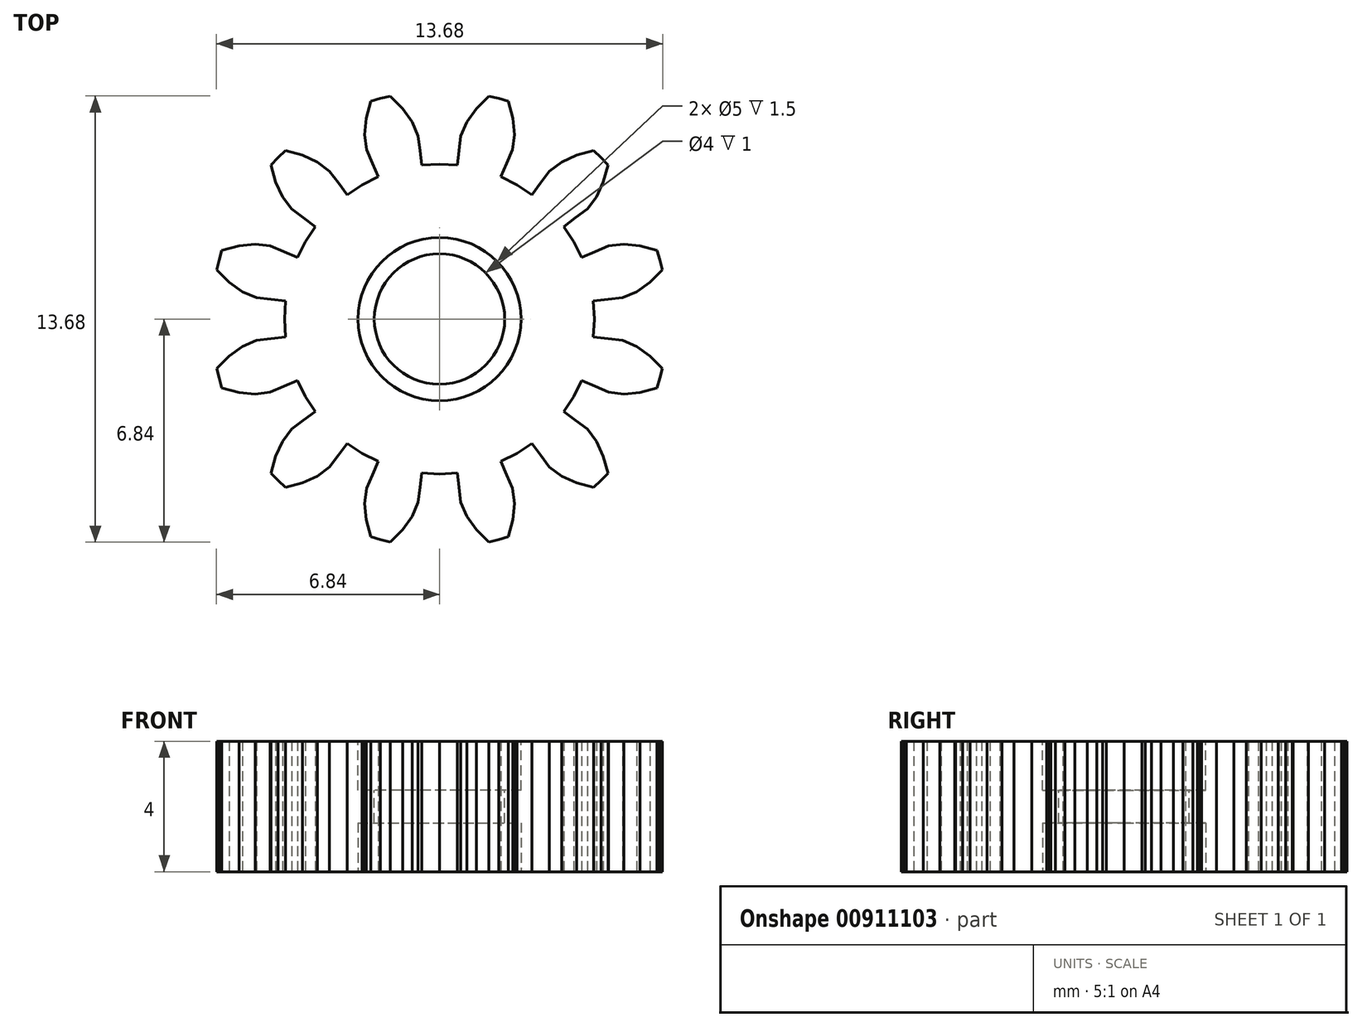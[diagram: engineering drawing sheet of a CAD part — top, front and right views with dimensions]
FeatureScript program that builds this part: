
annotation { "Feature Type Name" : "Feature", "Feature Type Description" : "" }
export const myFeature = defineFeature(function(context is Context, id is Id, definition is map)
    precondition{}
    {
        {
            var Q0;
            Q0=qCreatedBy(makeId("Top.planeOp"),FACE);
            var sketch = newSketch(context, id + "F0", { "sketchPlane" : qUnion([Q0])});
            skLineSegment(sketch, "E0", {"start": v(4.75, 0) * mm, "end": v(4.72, 0.55) * mm});
            skLineSegment(sketch, "E1", {"start": v(4.72, 0.55) * mm, "end": v(5.17, 0.6) * mm});
            skLineSegment(sketch, "E2", {"start": v(5.17, 0.6) * mm, "end": v(5.61, 0.65) * mm});
            skLineSegment(sketch, "E3", {"start": v(5.61, 0.65) * mm, "end": v(6.04, 0.84) * mm});
            skLineSegment(sketch, "E4", {"start": v(6.04, 0.84) * mm, "end": v(6.45, 1.13) * mm});
            skLineSegment(sketch, "E5", {"start": v(6.45, 1.13) * mm, "end": v(6.84, 1.51) * mm});
            skLineSegment(sketch, "E6", {"start": v(6.84, 1.51) * mm, "end": v(6.76, 1.81) * mm});
            skLineSegment(sketch, "E7", {"start": v(6.76, 1.81) * mm, "end": v(6.67, 2.1) * mm});
            skLineSegment(sketch, "E8", {"start": v(6.67, 2.1) * mm, "end": v(6.15, 2.25) * mm});
            skLineSegment(sketch, "E9", {"start": v(6.15, 2.25) * mm, "end": v(5.65, 2.3) * mm});
            skLineSegment(sketch, "E10", {"start": v(5.65, 2.3) * mm, "end": v(5.19, 2.24) * mm});
            skLineSegment(sketch, "E11", {"start": v(5.19, 2.24) * mm, "end": v(4.77, 2.06) * mm});
            skLineSegment(sketch, "E12", {"start": v(4.77, 2.06) * mm, "end": v(4.36, 1.88) * mm});
            skLineSegment(sketch, "E13", {"start": v(4.36, 1.88) * mm, "end": v(4.11, 2.38) * mm});
            skLineSegment(sketch, "E14", {"start": v(4.11, 2.38) * mm, "end": v(3.81, 2.84) * mm});
            skLineSegment(sketch, "E15", {"start": v(3.81, 2.84) * mm, "end": v(4.17, 3.1) * mm});
            skLineSegment(sketch, "E16", {"start": v(4.17, 3.1) * mm, "end": v(4.53, 3.37) * mm});
            skLineSegment(sketch, "E17", {"start": v(4.53, 3.37) * mm, "end": v(4.82, 3.74) * mm});
            skLineSegment(sketch, "E18", {"start": v(4.82, 3.74) * mm, "end": v(5.02, 4.2) * mm});
            skLineSegment(sketch, "E19", {"start": v(5.02, 4.2) * mm, "end": v(5.16, 4.73) * mm});
            skLineSegment(sketch, "E20", {"start": v(5.16, 4.73) * mm, "end": v(4.95, 4.95) * mm});
            skLineSegment(sketch, "E21", {"start": v(4.95, 4.95) * mm, "end": v(4.73, 5.16) * mm});
            skLineSegment(sketch, "E22", {"start": v(4.73, 5.16) * mm, "end": v(4.2, 5.02) * mm});
            skLineSegment(sketch, "E23", {"start": v(4.2, 5.02) * mm, "end": v(3.74, 4.82) * mm});
            skLineSegment(sketch, "E24", {"start": v(3.74, 4.82) * mm, "end": v(3.37, 4.53) * mm});
            skLineSegment(sketch, "E25", {"start": v(3.37, 4.53) * mm, "end": v(3.1, 4.17) * mm});
            skLineSegment(sketch, "E26", {"start": v(3.1, 4.17) * mm, "end": v(2.84, 3.81) * mm});
            skLineSegment(sketch, "E27", {"start": v(2.84, 3.81) * mm, "end": v(2.38, 4.11) * mm});
            skLineSegment(sketch, "E28", {"start": v(2.38, 4.11) * mm, "end": v(1.88, 4.36) * mm});
            skLineSegment(sketch, "E29", {"start": v(1.88, 4.36) * mm, "end": v(2.06, 4.77) * mm});
            skLineSegment(sketch, "E30", {"start": v(2.06, 4.77) * mm, "end": v(2.24, 5.19) * mm});
            skLineSegment(sketch, "E31", {"start": v(2.24, 5.19) * mm, "end": v(2.3, 5.65) * mm});
            skLineSegment(sketch, "E32", {"start": v(2.3, 5.65) * mm, "end": v(2.25, 6.15) * mm});
            skLineSegment(sketch, "E33", {"start": v(2.25, 6.15) * mm, "end": v(2.1, 6.67) * mm});
            skLineSegment(sketch, "E34", {"start": v(2.1, 6.67) * mm, "end": v(1.81, 6.76) * mm});
            skLineSegment(sketch, "E35", {"start": v(1.81, 6.76) * mm, "end": v(1.51, 6.84) * mm});
            skLineSegment(sketch, "E36", {"start": v(1.51, 6.84) * mm, "end": v(1.13, 6.45) * mm});
            skLineSegment(sketch, "E37", {"start": v(1.13, 6.45) * mm, "end": v(0.84, 6.04) * mm});
            skLineSegment(sketch, "E38", {"start": v(0.84, 6.04) * mm, "end": v(0.65, 5.61) * mm});
            skLineSegment(sketch, "E39", {"start": v(0.65, 5.61) * mm, "end": v(0.6, 5.17) * mm});
            skLineSegment(sketch, "E40", {"start": v(0.6, 5.17) * mm, "end": v(0.55, 4.72) * mm});
            skLineSegment(sketch, "E41", {"start": v(0.55, 4.72) * mm, "end": v(0, 4.75) * mm});
            skLineSegment(sketch, "E42", {"start": v(0, 4.75) * mm, "end": v(-0.55, 4.72) * mm});
            skLineSegment(sketch, "E43", {"start": v(-0.55, 4.72) * mm, "end": v(-0.6, 5.17) * mm});
            skLineSegment(sketch, "E44", {"start": v(-0.6, 5.17) * mm, "end": v(-0.65, 5.61) * mm});
            skLineSegment(sketch, "E45", {"start": v(-0.65, 5.61) * mm, "end": v(-0.84, 6.04) * mm});
            skLineSegment(sketch, "E46", {"start": v(-0.84, 6.04) * mm, "end": v(-1.13, 6.45) * mm});
            skLineSegment(sketch, "E47", {"start": v(-1.13, 6.45) * mm, "end": v(-1.51, 6.84) * mm});
            skLineSegment(sketch, "E48", {"start": v(-1.51, 6.84) * mm, "end": v(-1.81, 6.76) * mm});
            skLineSegment(sketch, "E49", {"start": v(-1.81, 6.76) * mm, "end": v(-2.1, 6.67) * mm});
            skLineSegment(sketch, "E50", {"start": v(-2.1, 6.67) * mm, "end": v(-2.25, 6.15) * mm});
            skLineSegment(sketch, "E51", {"start": v(-2.25, 6.15) * mm, "end": v(-2.3, 5.65) * mm});
            skLineSegment(sketch, "E52", {"start": v(-2.3, 5.65) * mm, "end": v(-2.24, 5.19) * mm});
            skLineSegment(sketch, "E53", {"start": v(-2.24, 5.19) * mm, "end": v(-2.06, 4.77) * mm});
            skLineSegment(sketch, "E54", {"start": v(-2.06, 4.77) * mm, "end": v(-1.88, 4.36) * mm});
            skLineSegment(sketch, "E55", {"start": v(-1.88, 4.36) * mm, "end": v(-2.38, 4.11) * mm});
            skLineSegment(sketch, "E56", {"start": v(-2.38, 4.11) * mm, "end": v(-2.84, 3.81) * mm});
            skLineSegment(sketch, "E57", {"start": v(-2.84, 3.81) * mm, "end": v(-3.1, 4.17) * mm});
            skLineSegment(sketch, "E58", {"start": v(-3.1, 4.17) * mm, "end": v(-3.37, 4.53) * mm});
            skLineSegment(sketch, "E59", {"start": v(-3.37, 4.53) * mm, "end": v(-3.74, 4.82) * mm});
            skLineSegment(sketch, "E60", {"start": v(-3.74, 4.82) * mm, "end": v(-4.2, 5.02) * mm});
            skLineSegment(sketch, "E61", {"start": v(-4.2, 5.02) * mm, "end": v(-4.73, 5.16) * mm});
            skLineSegment(sketch, "E62", {"start": v(-4.73, 5.16) * mm, "end": v(-4.95, 4.95) * mm});
            skLineSegment(sketch, "E63", {"start": v(-4.95, 4.95) * mm, "end": v(-5.16, 4.73) * mm});
            skLineSegment(sketch, "E64", {"start": v(-5.16, 4.73) * mm, "end": v(-5.02, 4.2) * mm});
            skLineSegment(sketch, "E65", {"start": v(-5.02, 4.2) * mm, "end": v(-4.82, 3.74) * mm});
            skLineSegment(sketch, "E66", {"start": v(-4.82, 3.74) * mm, "end": v(-4.53, 3.37) * mm});
            skLineSegment(sketch, "E67", {"start": v(-4.53, 3.37) * mm, "end": v(-4.17, 3.1) * mm});
            skLineSegment(sketch, "E68", {"start": v(-4.17, 3.1) * mm, "end": v(-3.81, 2.84) * mm});
            skLineSegment(sketch, "E69", {"start": v(-3.81, 2.84) * mm, "end": v(-4.11, 2.38) * mm});
            skLineSegment(sketch, "E70", {"start": v(-4.11, 2.38) * mm, "end": v(-4.36, 1.88) * mm});
            skLineSegment(sketch, "E71", {"start": v(-4.36, 1.88) * mm, "end": v(-4.77, 2.06) * mm});
            skLineSegment(sketch, "E72", {"start": v(-4.77, 2.06) * mm, "end": v(-5.19, 2.24) * mm});
            skLineSegment(sketch, "E73", {"start": v(-5.19, 2.24) * mm, "end": v(-5.65, 2.3) * mm});
            skLineSegment(sketch, "E74", {"start": v(-5.65, 2.3) * mm, "end": v(-6.15, 2.25) * mm});
            skLineSegment(sketch, "E75", {"start": v(-6.15, 2.25) * mm, "end": v(-6.67, 2.1) * mm});
            skLineSegment(sketch, "E76", {"start": v(-6.67, 2.1) * mm, "end": v(-6.76, 1.81) * mm});
            skLineSegment(sketch, "E77", {"start": v(-6.76, 1.81) * mm, "end": v(-6.84, 1.51) * mm});
            skLineSegment(sketch, "E78", {"start": v(-6.84, 1.51) * mm, "end": v(-6.45, 1.13) * mm});
            skLineSegment(sketch, "E79", {"start": v(-6.45, 1.13) * mm, "end": v(-6.04, 0.84) * mm});
            skLineSegment(sketch, "E80", {"start": v(-6.04, 0.84) * mm, "end": v(-5.61, 0.65) * mm});
            skLineSegment(sketch, "E81", {"start": v(-5.61, 0.65) * mm, "end": v(-5.17, 0.6) * mm});
            skLineSegment(sketch, "E82", {"start": v(-5.17, 0.6) * mm, "end": v(-4.72, 0.55) * mm});
            skLineSegment(sketch, "E83", {"start": v(-4.72, 0.55) * mm, "end": v(-4.75, 0) * mm});
            skLineSegment(sketch, "E84", {"start": v(-4.75, 0) * mm, "end": v(-4.72, -0.55) * mm});
            skLineSegment(sketch, "E85", {"start": v(-4.72, -0.55) * mm, "end": v(-5.17, -0.6) * mm});
            skLineSegment(sketch, "E86", {"start": v(-5.17, -0.6) * mm, "end": v(-5.61, -0.65) * mm});
            skLineSegment(sketch, "E87", {"start": v(-5.61, -0.65) * mm, "end": v(-6.04, -0.84) * mm});
            skLineSegment(sketch, "E88", {"start": v(-6.04, -0.84) * mm, "end": v(-6.45, -1.13) * mm});
            skLineSegment(sketch, "E89", {"start": v(-6.45, -1.13) * mm, "end": v(-6.84, -1.51) * mm});
            skLineSegment(sketch, "E90", {"start": v(-6.84, -1.51) * mm, "end": v(-6.76, -1.81) * mm});
            skLineSegment(sketch, "E91", {"start": v(-6.76, -1.81) * mm, "end": v(-6.67, -2.1) * mm});
            skLineSegment(sketch, "E92", {"start": v(-6.67, -2.1) * mm, "end": v(-6.15, -2.25) * mm});
            skLineSegment(sketch, "E93", {"start": v(-6.15, -2.25) * mm, "end": v(-5.65, -2.3) * mm});
            skLineSegment(sketch, "E94", {"start": v(-5.65, -2.3) * mm, "end": v(-5.19, -2.24) * mm});
            skLineSegment(sketch, "E95", {"start": v(-5.19, -2.24) * mm, "end": v(-4.77, -2.06) * mm});
            skLineSegment(sketch, "E96", {"start": v(-4.77, -2.06) * mm, "end": v(-4.36, -1.88) * mm});
            skLineSegment(sketch, "E97", {"start": v(-4.36, -1.88) * mm, "end": v(-4.11, -2.38) * mm});
            skLineSegment(sketch, "E98", {"start": v(-4.11, -2.38) * mm, "end": v(-3.81, -2.84) * mm});
            skLineSegment(sketch, "E99", {"start": v(-3.81, -2.84) * mm, "end": v(-4.17, -3.1) * mm});
            skLineSegment(sketch, "E100", {"start": v(-4.17, -3.1) * mm, "end": v(-4.53, -3.37) * mm});
            skLineSegment(sketch, "E101", {"start": v(-4.53, -3.37) * mm, "end": v(-4.82, -3.74) * mm});
            skLineSegment(sketch, "E102", {"start": v(-4.82, -3.74) * mm, "end": v(-5.02, -4.2) * mm});
            skLineSegment(sketch, "E103", {"start": v(-5.02, -4.2) * mm, "end": v(-5.16, -4.73) * mm});
            skLineSegment(sketch, "E104", {"start": v(-5.16, -4.73) * mm, "end": v(-4.95, -4.95) * mm});
            skLineSegment(sketch, "E105", {"start": v(-4.95, -4.95) * mm, "end": v(-4.73, -5.16) * mm});
            skLineSegment(sketch, "E106", {"start": v(-4.73, -5.16) * mm, "end": v(-4.2, -5.02) * mm});
            skLineSegment(sketch, "E107", {"start": v(-4.2, -5.02) * mm, "end": v(-3.74, -4.82) * mm});
            skLineSegment(sketch, "E108", {"start": v(-3.74, -4.82) * mm, "end": v(-3.37, -4.53) * mm});
            skLineSegment(sketch, "E109", {"start": v(-3.37, -4.53) * mm, "end": v(-3.1, -4.17) * mm});
            skLineSegment(sketch, "E110", {"start": v(-3.1, -4.17) * mm, "end": v(-2.84, -3.81) * mm});
            skLineSegment(sketch, "E111", {"start": v(-2.84, -3.81) * mm, "end": v(-2.38, -4.11) * mm});
            skLineSegment(sketch, "E112", {"start": v(-2.38, -4.11) * mm, "end": v(-1.88, -4.36) * mm});
            skLineSegment(sketch, "E113", {"start": v(-1.88, -4.36) * mm, "end": v(-2.06, -4.77) * mm});
            skLineSegment(sketch, "E114", {"start": v(-2.06, -4.77) * mm, "end": v(-2.24, -5.19) * mm});
            skLineSegment(sketch, "E115", {"start": v(-2.24, -5.19) * mm, "end": v(-2.3, -5.65) * mm});
            skLineSegment(sketch, "E116", {"start": v(-2.3, -5.65) * mm, "end": v(-2.25, -6.15) * mm});
            skLineSegment(sketch, "E117", {"start": v(-2.25, -6.15) * mm, "end": v(-2.1, -6.67) * mm});
            skLineSegment(sketch, "E118", {"start": v(-2.1, -6.67) * mm, "end": v(-1.81, -6.76) * mm});
            skLineSegment(sketch, "E119", {"start": v(-1.81, -6.76) * mm, "end": v(-1.51, -6.84) * mm});
            skLineSegment(sketch, "E120", {"start": v(-1.51, -6.84) * mm, "end": v(-1.13, -6.45) * mm});
            skLineSegment(sketch, "E121", {"start": v(-1.13, -6.45) * mm, "end": v(-0.84, -6.04) * mm});
            skLineSegment(sketch, "E122", {"start": v(-0.84, -6.04) * mm, "end": v(-0.65, -5.61) * mm});
            skLineSegment(sketch, "E123", {"start": v(-0.65, -5.61) * mm, "end": v(-0.6, -5.17) * mm});
            skLineSegment(sketch, "E124", {"start": v(-0.6, -5.17) * mm, "end": v(-0.55, -4.72) * mm});
            skLineSegment(sketch, "E125", {"start": v(-0.55, -4.72) * mm, "end": v(0, -4.75) * mm});
            skLineSegment(sketch, "E126", {"start": v(0, -4.75) * mm, "end": v(0.55, -4.72) * mm});
            skLineSegment(sketch, "E127", {"start": v(0.55, -4.72) * mm, "end": v(0.6, -5.17) * mm});
            skLineSegment(sketch, "E128", {"start": v(0.6, -5.17) * mm, "end": v(0.65, -5.61) * mm});
            skLineSegment(sketch, "E129", {"start": v(0.65, -5.61) * mm, "end": v(0.84, -6.04) * mm});
            skLineSegment(sketch, "E130", {"start": v(0.84, -6.04) * mm, "end": v(1.13, -6.45) * mm});
            skLineSegment(sketch, "E131", {"start": v(1.13, -6.45) * mm, "end": v(1.51, -6.84) * mm});
            skLineSegment(sketch, "E132", {"start": v(1.51, -6.84) * mm, "end": v(1.81, -6.76) * mm});
            skLineSegment(sketch, "E133", {"start": v(1.81, -6.76) * mm, "end": v(2.1, -6.67) * mm});
            skLineSegment(sketch, "E134", {"start": v(2.1, -6.67) * mm, "end": v(2.25, -6.15) * mm});
            skLineSegment(sketch, "E135", {"start": v(2.25, -6.15) * mm, "end": v(2.3, -5.65) * mm});
            skLineSegment(sketch, "E136", {"start": v(2.3, -5.65) * mm, "end": v(2.24, -5.19) * mm});
            skLineSegment(sketch, "E137", {"start": v(2.24, -5.19) * mm, "end": v(2.06, -4.77) * mm});
            skLineSegment(sketch, "E138", {"start": v(2.06, -4.77) * mm, "end": v(1.88, -4.36) * mm});
            skLineSegment(sketch, "E139", {"start": v(1.88, -4.36) * mm, "end": v(2.38, -4.11) * mm});
            skLineSegment(sketch, "E140", {"start": v(2.38, -4.11) * mm, "end": v(2.84, -3.81) * mm});
            skLineSegment(sketch, "E141", {"start": v(2.84, -3.81) * mm, "end": v(3.1, -4.17) * mm});
            skLineSegment(sketch, "E142", {"start": v(3.1, -4.17) * mm, "end": v(3.37, -4.53) * mm});
            skLineSegment(sketch, "E143", {"start": v(3.37, -4.53) * mm, "end": v(3.74, -4.82) * mm});
            skLineSegment(sketch, "E144", {"start": v(3.74, -4.82) * mm, "end": v(4.2, -5.02) * mm});
            skLineSegment(sketch, "E145", {"start": v(4.2, -5.02) * mm, "end": v(4.73, -5.16) * mm});
            skLineSegment(sketch, "E146", {"start": v(4.73, -5.16) * mm, "end": v(4.95, -4.95) * mm});
            skLineSegment(sketch, "E147", {"start": v(4.95, -4.95) * mm, "end": v(5.16, -4.73) * mm});
            skLineSegment(sketch, "E148", {"start": v(5.16, -4.73) * mm, "end": v(5.02, -4.2) * mm});
            skLineSegment(sketch, "E149", {"start": v(5.02, -4.2) * mm, "end": v(4.82, -3.74) * mm});
            skLineSegment(sketch, "E150", {"start": v(4.82, -3.74) * mm, "end": v(4.53, -3.37) * mm});
            skLineSegment(sketch, "E151", {"start": v(4.53, -3.37) * mm, "end": v(4.17, -3.1) * mm});
            skLineSegment(sketch, "E152", {"start": v(4.17, -3.1) * mm, "end": v(3.81, -2.84) * mm});
            skLineSegment(sketch, "E153", {"start": v(3.81, -2.84) * mm, "end": v(4.11, -2.38) * mm});
            skLineSegment(sketch, "E154", {"start": v(4.11, -2.38) * mm, "end": v(4.36, -1.88) * mm});
            skLineSegment(sketch, "E155", {"start": v(4.36, -1.88) * mm, "end": v(4.77, -2.06) * mm});
            skLineSegment(sketch, "E156", {"start": v(4.77, -2.06) * mm, "end": v(5.19, -2.24) * mm});
            skLineSegment(sketch, "E157", {"start": v(5.19, -2.24) * mm, "end": v(5.65, -2.3) * mm});
            skLineSegment(sketch, "E158", {"start": v(5.65, -2.3) * mm, "end": v(6.15, -2.25) * mm});
            skLineSegment(sketch, "E159", {"start": v(6.15, -2.25) * mm, "end": v(6.67, -2.1) * mm});
            skLineSegment(sketch, "E160", {"start": v(6.67, -2.1) * mm, "end": v(6.76, -1.81) * mm});
            skLineSegment(sketch, "E161", {"start": v(6.76, -1.81) * mm, "end": v(6.84, -1.51) * mm});
            skLineSegment(sketch, "E162", {"start": v(6.84, -1.51) * mm, "end": v(6.45, -1.13) * mm});
            skLineSegment(sketch, "E163", {"start": v(6.45, -1.13) * mm, "end": v(6.04, -0.84) * mm});
            skLineSegment(sketch, "E164", {"start": v(6.04, -0.84) * mm, "end": v(5.61, -0.65) * mm});
            skLineSegment(sketch, "E165", {"start": v(5.61, -0.65) * mm, "end": v(5.17, -0.6) * mm});
            skLineSegment(sketch, "E166", {"start": v(5.17, -0.6) * mm, "end": v(4.72, -0.55) * mm});
            skLineSegment(sketch, "E167", {"start": v(4.75, 0) * mm, "end": v(4.72, -0.55) * mm});
            skSolve(sketch);
        }
        {
            var Q0;
            Q0 = qSketchRegion(id + "F0", true);
            extrude(context, id + "F1", {"entities" : qUnion([Q0]), "depth" : 4 * mm, "offsetDistance" : 25 * mm});
        }
        {
            var Q0;
            Q0=makeQuery(id+"F1.opExtrude","CAP_FACE",FACE,{"disambiguationData":[OSD([sQuery(id+"F0.wireOp",EDGE,"E0"),sQuery(id+"F0.wireOp",EDGE,"E1"),sQuery(id+"F0.wireOp",EDGE,"E2"),sQuery(id+"F0.wireOp",EDGE,"E3"),sQuery(id+"F0.wireOp",EDGE,"E4"),sQuery(id+"F0.wireOp",EDGE,"E5"),sQuery(id+"F0.wireOp",EDGE,"E6"),sQuery(id+"F0.wireOp",EDGE,"E7"),sQuery(id+"F0.wireOp",EDGE,"E8"),sQuery(id+"F0.wireOp",EDGE,"E9"),sQuery(id+"F0.wireOp",EDGE,"E10"),sQuery(id+"F0.wireOp",EDGE,"E11"),sQuery(id+"F0.wireOp",EDGE,"E12"),sQuery(id+"F0.wireOp",EDGE,"E13"),sQuery(id+"F0.wireOp",EDGE,"E14"),sQuery(id+"F0.wireOp",EDGE,"E15"),sQuery(id+"F0.wireOp",EDGE,"E16"),sQuery(id+"F0.wireOp",EDGE,"E17"),sQuery(id+"F0.wireOp",EDGE,"E18"),sQuery(id+"F0.wireOp",EDGE,"E19"),sQuery(id+"F0.wireOp",EDGE,"E20"),sQuery(id+"F0.wireOp",EDGE,"E21"),sQuery(id+"F0.wireOp",EDGE,"E22"),sQuery(id+"F0.wireOp",EDGE,"E23"),sQuery(id+"F0.wireOp",EDGE,"E24"),sQuery(id+"F0.wireOp",EDGE,"E25"),sQuery(id+"F0.wireOp",EDGE,"E26"),sQuery(id+"F0.wireOp",EDGE,"E27"),sQuery(id+"F0.wireOp",EDGE,"E28"),sQuery(id+"F0.wireOp",EDGE,"E29"),sQuery(id+"F0.wireOp",EDGE,"E30"),sQuery(id+"F0.wireOp",EDGE,"E31"),sQuery(id+"F0.wireOp",EDGE,"E32"),sQuery(id+"F0.wireOp",EDGE,"E33"),sQuery(id+"F0.wireOp",EDGE,"E34"),sQuery(id+"F0.wireOp",EDGE,"E35"),sQuery(id+"F0.wireOp",EDGE,"E36"),sQuery(id+"F0.wireOp",EDGE,"E37"),sQuery(id+"F0.wireOp",EDGE,"E38"),sQuery(id+"F0.wireOp",EDGE,"E39"),sQuery(id+"F0.wireOp",EDGE,"E40"),sQuery(id+"F0.wireOp",EDGE,"E41"),sQuery(id+"F0.wireOp",EDGE,"E42"),sQuery(id+"F0.wireOp",EDGE,"E43"),sQuery(id+"F0.wireOp",EDGE,"E44"),sQuery(id+"F0.wireOp",EDGE,"E45"),sQuery(id+"F0.wireOp",EDGE,"E46"),sQuery(id+"F0.wireOp",EDGE,"E47"),sQuery(id+"F0.wireOp",EDGE,"E48"),sQuery(id+"F0.wireOp",EDGE,"E49"),sQuery(id+"F0.wireOp",EDGE,"E50"),sQuery(id+"F0.wireOp",EDGE,"E51"),sQuery(id+"F0.wireOp",EDGE,"E52"),sQuery(id+"F0.wireOp",EDGE,"E53"),sQuery(id+"F0.wireOp",EDGE,"E54"),sQuery(id+"F0.wireOp",EDGE,"E55"),sQuery(id+"F0.wireOp",EDGE,"E56"),sQuery(id+"F0.wireOp",EDGE,"E57"),sQuery(id+"F0.wireOp",EDGE,"E58"),sQuery(id+"F0.wireOp",EDGE,"E59"),sQuery(id+"F0.wireOp",EDGE,"E60"),sQuery(id+"F0.wireOp",EDGE,"E61"),sQuery(id+"F0.wireOp",EDGE,"E62"),sQuery(id+"F0.wireOp",EDGE,"E63"),sQuery(id+"F0.wireOp",EDGE,"E64"),sQuery(id+"F0.wireOp",EDGE,"E65"),sQuery(id+"F0.wireOp",EDGE,"E66"),sQuery(id+"F0.wireOp",EDGE,"E67"),sQuery(id+"F0.wireOp",EDGE,"E68"),sQuery(id+"F0.wireOp",EDGE,"E69"),sQuery(id+"F0.wireOp",EDGE,"E70"),sQuery(id+"F0.wireOp",EDGE,"E71"),sQuery(id+"F0.wireOp",EDGE,"E72"),sQuery(id+"F0.wireOp",EDGE,"E73"),sQuery(id+"F0.wireOp",EDGE,"E74"),sQuery(id+"F0.wireOp",EDGE,"E75"),sQuery(id+"F0.wireOp",EDGE,"E76"),sQuery(id+"F0.wireOp",EDGE,"E77"),sQuery(id+"F0.wireOp",EDGE,"E78"),sQuery(id+"F0.wireOp",EDGE,"E79"),sQuery(id+"F0.wireOp",EDGE,"E80"),sQuery(id+"F0.wireOp",EDGE,"E81"),sQuery(id+"F0.wireOp",EDGE,"E82"),sQuery(id+"F0.wireOp",EDGE,"E83"),sQuery(id+"F0.wireOp",EDGE,"E84"),sQuery(id+"F0.wireOp",EDGE,"E85"),sQuery(id+"F0.wireOp",EDGE,"E86"),sQuery(id+"F0.wireOp",EDGE,"E87"),sQuery(id+"F0.wireOp",EDGE,"E88"),sQuery(id+"F0.wireOp",EDGE,"E89"),sQuery(id+"F0.wireOp",EDGE,"E90"),sQuery(id+"F0.wireOp",EDGE,"E91"),sQuery(id+"F0.wireOp",EDGE,"E92"),sQuery(id+"F0.wireOp",EDGE,"E93"),sQuery(id+"F0.wireOp",EDGE,"E94"),sQuery(id+"F0.wireOp",EDGE,"E95"),sQuery(id+"F0.wireOp",EDGE,"E96"),sQuery(id+"F0.wireOp",EDGE,"E97"),sQuery(id+"F0.wireOp",EDGE,"E98"),sQuery(id+"F0.wireOp",EDGE,"E99"),sQuery(id+"F0.wireOp",EDGE,"E100"),sQuery(id+"F0.wireOp",EDGE,"E101"),sQuery(id+"F0.wireOp",EDGE,"E102"),sQuery(id+"F0.wireOp",EDGE,"E103"),sQuery(id+"F0.wireOp",EDGE,"E104"),sQuery(id+"F0.wireOp",EDGE,"E105"),sQuery(id+"F0.wireOp",EDGE,"E106"),sQuery(id+"F0.wireOp",EDGE,"E107"),sQuery(id+"F0.wireOp",EDGE,"E108"),sQuery(id+"F0.wireOp",EDGE,"E109"),sQuery(id+"F0.wireOp",EDGE,"E110"),sQuery(id+"F0.wireOp",EDGE,"E111"),sQuery(id+"F0.wireOp",EDGE,"E112"),sQuery(id+"F0.wireOp",EDGE,"E113"),sQuery(id+"F0.wireOp",EDGE,"E114"),sQuery(id+"F0.wireOp",EDGE,"E115"),sQuery(id+"F0.wireOp",EDGE,"E116"),sQuery(id+"F0.wireOp",EDGE,"E117"),sQuery(id+"F0.wireOp",EDGE,"E118"),sQuery(id+"F0.wireOp",EDGE,"E119"),sQuery(id+"F0.wireOp",EDGE,"E120"),sQuery(id+"F0.wireOp",EDGE,"E121"),sQuery(id+"F0.wireOp",EDGE,"E122"),sQuery(id+"F0.wireOp",EDGE,"E123"),sQuery(id+"F0.wireOp",EDGE,"E124"),sQuery(id+"F0.wireOp",EDGE,"E125"),sQuery(id+"F0.wireOp",EDGE,"E126"),sQuery(id+"F0.wireOp",EDGE,"E127"),sQuery(id+"F0.wireOp",EDGE,"E128"),sQuery(id+"F0.wireOp",EDGE,"E129"),sQuery(id+"F0.wireOp",EDGE,"E130"),sQuery(id+"F0.wireOp",EDGE,"E131"),sQuery(id+"F0.wireOp",EDGE,"E132"),sQuery(id+"F0.wireOp",EDGE,"E133"),sQuery(id+"F0.wireOp",EDGE,"E134"),sQuery(id+"F0.wireOp",EDGE,"E135"),sQuery(id+"F0.wireOp",EDGE,"E136"),sQuery(id+"F0.wireOp",EDGE,"E137"),sQuery(id+"F0.wireOp",EDGE,"E138"),sQuery(id+"F0.wireOp",EDGE,"E139"),sQuery(id+"F0.wireOp",EDGE,"E140"),sQuery(id+"F0.wireOp",EDGE,"E141"),sQuery(id+"F0.wireOp",EDGE,"E142"),sQuery(id+"F0.wireOp",EDGE,"E143"),sQuery(id+"F0.wireOp",EDGE,"E144"),sQuery(id+"F0.wireOp",EDGE,"E145"),sQuery(id+"F0.wireOp",EDGE,"E146"),sQuery(id+"F0.wireOp",EDGE,"E147"),sQuery(id+"F0.wireOp",EDGE,"E148"),sQuery(id+"F0.wireOp",EDGE,"E149"),sQuery(id+"F0.wireOp",EDGE,"E150"),sQuery(id+"F0.wireOp",EDGE,"E151"),sQuery(id+"F0.wireOp",EDGE,"E152"),sQuery(id+"F0.wireOp",EDGE,"E153"),sQuery(id+"F0.wireOp",EDGE,"E154"),sQuery(id+"F0.wireOp",EDGE,"E155"),sQuery(id+"F0.wireOp",EDGE,"E156"),sQuery(id+"F0.wireOp",EDGE,"E157"),sQuery(id+"F0.wireOp",EDGE,"E158"),sQuery(id+"F0.wireOp",EDGE,"E159"),sQuery(id+"F0.wireOp",EDGE,"E160"),sQuery(id+"F0.wireOp",EDGE,"E161"),sQuery(id+"F0.wireOp",EDGE,"E162"),sQuery(id+"F0.wireOp",EDGE,"E163"),sQuery(id+"F0.wireOp",EDGE,"E164"),sQuery(id+"F0.wireOp",EDGE,"E165"),sQuery(id+"F0.wireOp",EDGE,"E166"),sQuery(id+"F0.wireOp",EDGE,"E167")])],"isStart":false});
            var sketch = newSketch(context, id + "F2", { "sketchPlane" : qUnion([Q0])});
            skCircle(sketch, "E168", {"center": v(0, 0) * mm, "radius": 2.5 * mm});
            skSolve(sketch);
        }
        {
            var Q0;
            Q0 = qSketchRegion(id + "F2", true);
            extrude(context, id + "F3", {"entities" : qUnion([Q0]), "operationType" : NewBodyOperationType.REMOVE, "oppositeDirection" : true, "depth" : 1.5 * mm, "offsetDistance" : 25 * mm});
        }
        {
            var Q0;
            Q0=makeQuery(id+"F1.opExtrude","CAP_FACE",FACE,{"disambiguationData":[OSD([sQuery(id+"F0.wireOp",EDGE,"E0"),sQuery(id+"F0.wireOp",EDGE,"E1"),sQuery(id+"F0.wireOp",EDGE,"E2"),sQuery(id+"F0.wireOp",EDGE,"E3"),sQuery(id+"F0.wireOp",EDGE,"E4"),sQuery(id+"F0.wireOp",EDGE,"E5"),sQuery(id+"F0.wireOp",EDGE,"E6"),sQuery(id+"F0.wireOp",EDGE,"E7"),sQuery(id+"F0.wireOp",EDGE,"E8"),sQuery(id+"F0.wireOp",EDGE,"E9"),sQuery(id+"F0.wireOp",EDGE,"E10"),sQuery(id+"F0.wireOp",EDGE,"E11"),sQuery(id+"F0.wireOp",EDGE,"E12"),sQuery(id+"F0.wireOp",EDGE,"E13"),sQuery(id+"F0.wireOp",EDGE,"E14"),sQuery(id+"F0.wireOp",EDGE,"E15"),sQuery(id+"F0.wireOp",EDGE,"E16"),sQuery(id+"F0.wireOp",EDGE,"E17"),sQuery(id+"F0.wireOp",EDGE,"E18"),sQuery(id+"F0.wireOp",EDGE,"E19"),sQuery(id+"F0.wireOp",EDGE,"E20"),sQuery(id+"F0.wireOp",EDGE,"E21"),sQuery(id+"F0.wireOp",EDGE,"E22"),sQuery(id+"F0.wireOp",EDGE,"E23"),sQuery(id+"F0.wireOp",EDGE,"E24"),sQuery(id+"F0.wireOp",EDGE,"E25"),sQuery(id+"F0.wireOp",EDGE,"E26"),sQuery(id+"F0.wireOp",EDGE,"E27"),sQuery(id+"F0.wireOp",EDGE,"E28"),sQuery(id+"F0.wireOp",EDGE,"E29"),sQuery(id+"F0.wireOp",EDGE,"E30"),sQuery(id+"F0.wireOp",EDGE,"E31"),sQuery(id+"F0.wireOp",EDGE,"E32"),sQuery(id+"F0.wireOp",EDGE,"E33"),sQuery(id+"F0.wireOp",EDGE,"E34"),sQuery(id+"F0.wireOp",EDGE,"E35"),sQuery(id+"F0.wireOp",EDGE,"E36"),sQuery(id+"F0.wireOp",EDGE,"E37"),sQuery(id+"F0.wireOp",EDGE,"E38"),sQuery(id+"F0.wireOp",EDGE,"E39"),sQuery(id+"F0.wireOp",EDGE,"E40"),sQuery(id+"F0.wireOp",EDGE,"E41"),sQuery(id+"F0.wireOp",EDGE,"E42"),sQuery(id+"F0.wireOp",EDGE,"E43"),sQuery(id+"F0.wireOp",EDGE,"E44"),sQuery(id+"F0.wireOp",EDGE,"E45"),sQuery(id+"F0.wireOp",EDGE,"E46"),sQuery(id+"F0.wireOp",EDGE,"E47"),sQuery(id+"F0.wireOp",EDGE,"E48"),sQuery(id+"F0.wireOp",EDGE,"E49"),sQuery(id+"F0.wireOp",EDGE,"E50"),sQuery(id+"F0.wireOp",EDGE,"E51"),sQuery(id+"F0.wireOp",EDGE,"E52"),sQuery(id+"F0.wireOp",EDGE,"E53"),sQuery(id+"F0.wireOp",EDGE,"E54"),sQuery(id+"F0.wireOp",EDGE,"E55"),sQuery(id+"F0.wireOp",EDGE,"E56"),sQuery(id+"F0.wireOp",EDGE,"E57"),sQuery(id+"F0.wireOp",EDGE,"E58"),sQuery(id+"F0.wireOp",EDGE,"E59"),sQuery(id+"F0.wireOp",EDGE,"E60"),sQuery(id+"F0.wireOp",EDGE,"E61"),sQuery(id+"F0.wireOp",EDGE,"E62"),sQuery(id+"F0.wireOp",EDGE,"E63"),sQuery(id+"F0.wireOp",EDGE,"E64"),sQuery(id+"F0.wireOp",EDGE,"E65"),sQuery(id+"F0.wireOp",EDGE,"E66"),sQuery(id+"F0.wireOp",EDGE,"E67"),sQuery(id+"F0.wireOp",EDGE,"E68"),sQuery(id+"F0.wireOp",EDGE,"E69"),sQuery(id+"F0.wireOp",EDGE,"E70"),sQuery(id+"F0.wireOp",EDGE,"E71"),sQuery(id+"F0.wireOp",EDGE,"E72"),sQuery(id+"F0.wireOp",EDGE,"E73"),sQuery(id+"F0.wireOp",EDGE,"E74"),sQuery(id+"F0.wireOp",EDGE,"E75"),sQuery(id+"F0.wireOp",EDGE,"E76"),sQuery(id+"F0.wireOp",EDGE,"E77"),sQuery(id+"F0.wireOp",EDGE,"E78"),sQuery(id+"F0.wireOp",EDGE,"E79"),sQuery(id+"F0.wireOp",EDGE,"E80"),sQuery(id+"F0.wireOp",EDGE,"E81"),sQuery(id+"F0.wireOp",EDGE,"E82"),sQuery(id+"F0.wireOp",EDGE,"E83"),sQuery(id+"F0.wireOp",EDGE,"E84"),sQuery(id+"F0.wireOp",EDGE,"E85"),sQuery(id+"F0.wireOp",EDGE,"E86"),sQuery(id+"F0.wireOp",EDGE,"E87"),sQuery(id+"F0.wireOp",EDGE,"E88"),sQuery(id+"F0.wireOp",EDGE,"E89"),sQuery(id+"F0.wireOp",EDGE,"E90"),sQuery(id+"F0.wireOp",EDGE,"E91"),sQuery(id+"F0.wireOp",EDGE,"E92"),sQuery(id+"F0.wireOp",EDGE,"E93"),sQuery(id+"F0.wireOp",EDGE,"E94"),sQuery(id+"F0.wireOp",EDGE,"E95"),sQuery(id+"F0.wireOp",EDGE,"E96"),sQuery(id+"F0.wireOp",EDGE,"E97"),sQuery(id+"F0.wireOp",EDGE,"E98"),sQuery(id+"F0.wireOp",EDGE,"E99"),sQuery(id+"F0.wireOp",EDGE,"E100"),sQuery(id+"F0.wireOp",EDGE,"E101"),sQuery(id+"F0.wireOp",EDGE,"E102"),sQuery(id+"F0.wireOp",EDGE,"E103"),sQuery(id+"F0.wireOp",EDGE,"E104"),sQuery(id+"F0.wireOp",EDGE,"E105"),sQuery(id+"F0.wireOp",EDGE,"E106"),sQuery(id+"F0.wireOp",EDGE,"E107"),sQuery(id+"F0.wireOp",EDGE,"E108"),sQuery(id+"F0.wireOp",EDGE,"E109"),sQuery(id+"F0.wireOp",EDGE,"E110"),sQuery(id+"F0.wireOp",EDGE,"E111"),sQuery(id+"F0.wireOp",EDGE,"E112"),sQuery(id+"F0.wireOp",EDGE,"E113"),sQuery(id+"F0.wireOp",EDGE,"E114"),sQuery(id+"F0.wireOp",EDGE,"E115"),sQuery(id+"F0.wireOp",EDGE,"E116"),sQuery(id+"F0.wireOp",EDGE,"E117"),sQuery(id+"F0.wireOp",EDGE,"E118"),sQuery(id+"F0.wireOp",EDGE,"E119"),sQuery(id+"F0.wireOp",EDGE,"E120"),sQuery(id+"F0.wireOp",EDGE,"E121"),sQuery(id+"F0.wireOp",EDGE,"E122"),sQuery(id+"F0.wireOp",EDGE,"E123"),sQuery(id+"F0.wireOp",EDGE,"E124"),sQuery(id+"F0.wireOp",EDGE,"E125"),sQuery(id+"F0.wireOp",EDGE,"E126"),sQuery(id+"F0.wireOp",EDGE,"E127"),sQuery(id+"F0.wireOp",EDGE,"E128"),sQuery(id+"F0.wireOp",EDGE,"E129"),sQuery(id+"F0.wireOp",EDGE,"E130"),sQuery(id+"F0.wireOp",EDGE,"E131"),sQuery(id+"F0.wireOp",EDGE,"E132"),sQuery(id+"F0.wireOp",EDGE,"E133"),sQuery(id+"F0.wireOp",EDGE,"E134"),sQuery(id+"F0.wireOp",EDGE,"E135"),sQuery(id+"F0.wireOp",EDGE,"E136"),sQuery(id+"F0.wireOp",EDGE,"E137"),sQuery(id+"F0.wireOp",EDGE,"E138"),sQuery(id+"F0.wireOp",EDGE,"E139"),sQuery(id+"F0.wireOp",EDGE,"E140"),sQuery(id+"F0.wireOp",EDGE,"E141"),sQuery(id+"F0.wireOp",EDGE,"E142"),sQuery(id+"F0.wireOp",EDGE,"E143"),sQuery(id+"F0.wireOp",EDGE,"E144"),sQuery(id+"F0.wireOp",EDGE,"E145"),sQuery(id+"F0.wireOp",EDGE,"E146"),sQuery(id+"F0.wireOp",EDGE,"E147"),sQuery(id+"F0.wireOp",EDGE,"E148"),sQuery(id+"F0.wireOp",EDGE,"E149"),sQuery(id+"F0.wireOp",EDGE,"E150"),sQuery(id+"F0.wireOp",EDGE,"E151"),sQuery(id+"F0.wireOp",EDGE,"E152"),sQuery(id+"F0.wireOp",EDGE,"E153"),sQuery(id+"F0.wireOp",EDGE,"E154"),sQuery(id+"F0.wireOp",EDGE,"E155"),sQuery(id+"F0.wireOp",EDGE,"E156"),sQuery(id+"F0.wireOp",EDGE,"E157"),sQuery(id+"F0.wireOp",EDGE,"E158"),sQuery(id+"F0.wireOp",EDGE,"E159"),sQuery(id+"F0.wireOp",EDGE,"E160"),sQuery(id+"F0.wireOp",EDGE,"E161"),sQuery(id+"F0.wireOp",EDGE,"E162"),sQuery(id+"F0.wireOp",EDGE,"E163"),sQuery(id+"F0.wireOp",EDGE,"E164"),sQuery(id+"F0.wireOp",EDGE,"E165"),sQuery(id+"F0.wireOp",EDGE,"E166"),sQuery(id+"F0.wireOp",EDGE,"E167")])],"isStart":true});
            var sketch = newSketch(context, id + "F4", { "sketchPlane" : qUnion([Q0])});
            skCircle(sketch, "E169", {"center": v(0, 0) * mm, "radius": 2.5 * mm});
            skSolve(sketch);
        }
        {
            var Q0;
            Q0 = qSketchRegion(id + "F4", true);
            extrude(context, id + "F5", {"entities" : qUnion([Q0]), "operationType" : NewBodyOperationType.REMOVE, "oppositeDirection" : true, "depth" : 1.5 * mm, "offsetDistance" : 25 * mm});
        }
        {
            var Q0;
            Q0=makeQuery(id+"F3.boolean.opBoolean","COPY",FACE,{"derivedFrom":makeQuery(id+"F3.opExtrude","CAP_FACE",FACE,{"disambiguationData":[OSD([sQuery(id+"F2.wireOp",EDGE,"E168")])],"isStart":false})});
            var sketch = newSketch(context, id + "F6", { "sketchPlane" : qUnion([Q0])});
            skCircle(sketch, "E170", {"center": v(0, 0) * mm, "radius": 2 * mm});
            skSolve(sketch);
        }
        {
            var Q0;
            Q0 = qSketchRegion(id + "F6", true);
            extrude(context, id + "F7", {"entities" : qUnion([Q0]), "operationType" : NewBodyOperationType.REMOVE, "oppositeDirection" : true, "depth" : 25 * mm, "offsetDistance" : 25 * mm});
        }
    });
